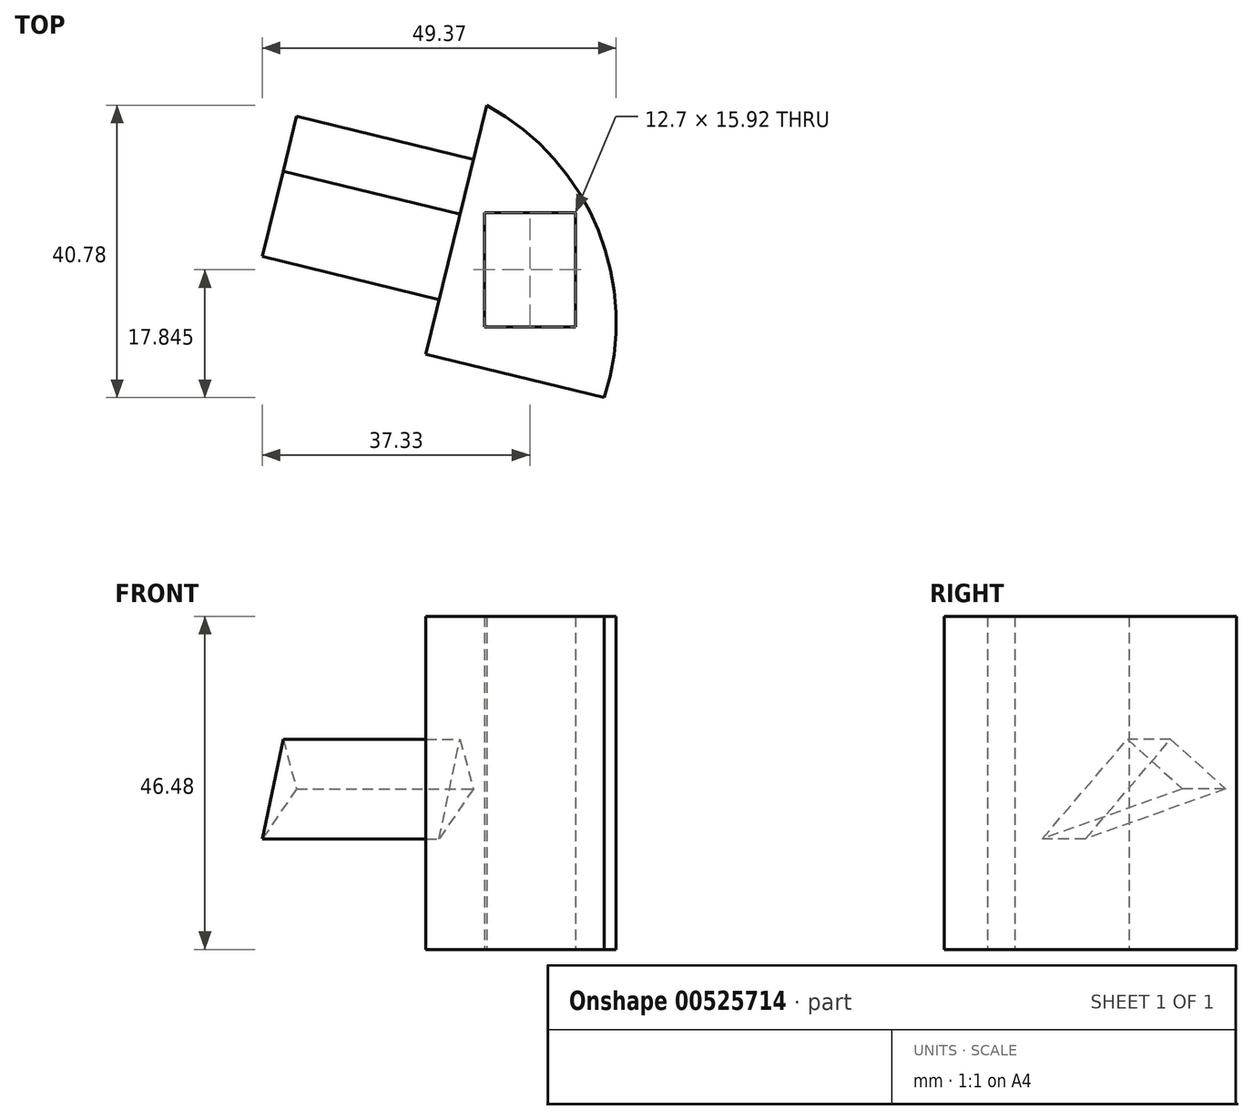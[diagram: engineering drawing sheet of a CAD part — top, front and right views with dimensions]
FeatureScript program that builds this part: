
annotation { "Feature Type Name" : "Feature", "Feature Type Description" : "" }
export const myFeature = defineFeature(function(context is Context, id is Id, definition is map)
    precondition{}
    {
        {
            var Q0;
            Q0=qCreatedBy(makeId("Top.planeOp"),FACE);
            var sketch = newSketch(context, id + "F0", { "sketchPlane" : qUnion([Q0])});
            skLineSegment(sketch, "E0", {"start": v(0.3, 20.36) * mm, "end": v(-8.17, -14.34) * mm});
            skLineSegment(sketch, "E1", {"start": v(-8.17, -14.34) * mm, "end": v(16.74, -20.42) * mm});
            skArc(sketch, "E2", {"start": v(16.74, -20.42) * mm, "mid": v(15.9, 2.94) * mm, "end": v(0.3, 20.36) * mm});
            skLineSegment(sketch, "E3.bottom", {"start": v(0, -10.54) * mm, "end": v(12.7, -10.54) * mm});
            skLineSegment(sketch, "E3.top", {"start": v(0, 5.39) * mm, "end": v(12.7, 5.39) * mm});
            skLineSegment(sketch, "E3.left", {"start": v(0, -10.54) * mm, "end": v(0, 5.39) * mm});
            skLineSegment(sketch, "E3.right", {"start": v(12.7, -10.54) * mm, "end": v(12.7, 5.39) * mm});
            skSolve(sketch);
        }
        {
            var Q0;
            Q0=makeQuery(id+"F0.imprint","IMPRINT",FACE,{"disambiguationData":[TD([[makeQuery(id+"F0.imprint","IMPRINT",EDGE,{"derivedFrom":sQuery(id+"F0.wireOp",EDGE,"E0")}),1.0]])]});
            extrude(context, id + "F1", {"entities" : qUnion([Q0]), "depth" : 46.48 * mm, "offsetDistance" : 25.4 * mm});
        }
        {
            var Q0;
            Q0=makeQuery(id+"F1.opExtrude","SWEPT_FACE",FACE,{"disambiguationData":[OSD([sQuery(id+"F0.wireOp",EDGE,"E0")])]});
            var sketch = newSketch(context, id + "F2", { "sketchPlane" : qUnion([Q0])});
            skLineSegment(sketch, "E4", {"start": v(-4.2, 29.33) * mm, "end": v(-12.1, 22.4) * mm});
            skLineSegment(sketch, "E5", {"start": v(-12.1, 22.4) * mm, "end": v(8.03, 15.41) * mm});
            skLineSegment(sketch, "E6", {"start": v(8.03, 15.41) * mm, "end": v(-4.2, 29.33) * mm});
            skSolve(sketch);
        }
        {
            var Q0;
            Q0=makeQuery(id+"F2.imprint","IMPRINT",FACE,{"disambiguationData":[TD([[makeQuery(id+"F2.imprint","IMPRINT",EDGE,{"derivedFrom":sQuery(id+"F2.wireOp",EDGE,"E4")}),1.0]])]});
            extrude(context, id + "F3", {"entities" : qUnion([Q0]), "operationType" : NewBodyOperationType.ADD, "depth" : 25.4 * mm, "offsetDistance" : 25.4 * mm});
        }
    });
